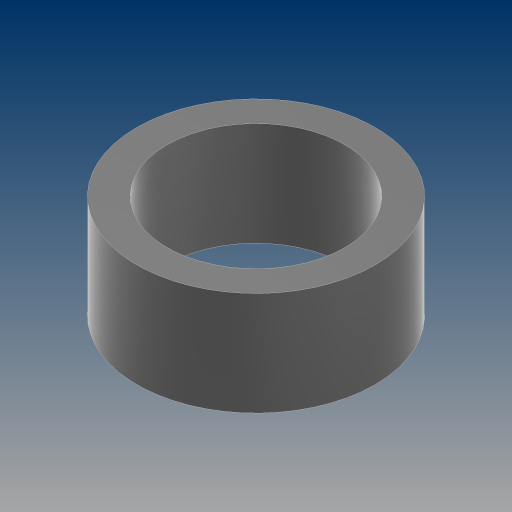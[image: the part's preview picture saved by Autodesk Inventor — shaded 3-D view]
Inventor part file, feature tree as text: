
AUTODESK INVENTOR PART (.ipt)
format: ipt  version: 2024.3 (Build 283343000, 343)  size: 110,080 bytes
history: native  units: in
note: dims shown in document units (in); Inventor stores cm internally (conversion verified against a paired STEP export)
features: extrude x1, sketch x1
ambient origin geometry x8: Origin, YZ Plane, XZ Plane, XY Plane, X Axis, Y Axis, Z Axis, Center Point
bodies: Solid1 (feature_tree)
feature tree (2):
  extrude  "Extrusion1"  Depth=0.326in
  sketch  "Sketch1"  dims[d0=0.56in d1=0.75in d2=0.326in d3=0.0in]
